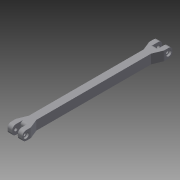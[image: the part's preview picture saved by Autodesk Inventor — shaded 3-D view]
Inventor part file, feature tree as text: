
AUTODESK INVENTOR PART (.ipt)
format: ipt  version: 2015 (Build 190159000, 159)  size: 167,424 bytes
history: native  units: mm
features: sketch x4, fillet x4, extrude x2, plane x2, mirror x2, loft x1, hole x1, other x1
ambient origin geometry x8: Origin, YZ Plane, XZ Plane, XY Plane, X Axis, Y Axis, Z Axis, Center Point
bodies: Solid1 (feature_tree)
feature tree (17):
  extrude  "Extrusion1"  Depth=10.0mm
  sketch  "Sketch2"  dims[d2=144.0mm d3=0.0mm d4=5.0mm]
  sketch  "Sketch3"  dims[d5=5.0mm d6=3.05mm d7=3.05mm d8=10.0mm]
  extrude  "Extrusion3"  Depth=5.0mm
  loft  "Loft2"
  plane  "Work Plane2"
  fillet  "Fillet4"  Radius=3.05mm
  fillet  "Fillet5"  Radius=10.0mm
  hole  "Hole1"  [1 undecoded]
  mirror  "Mirror2"
  plane  "Work Plane3"
  mirror  "Mirror3"
  fillet  "Fillet6"  [1 undecoded]
  fillet  "Fillet7"  Radius=4.0mm
  sketch  "Sketch1"  dims[d0=8.0mm d1=10.0mm]
  other  "Edges1"
  sketch  "Sketch5"  dims[d18=9.0mm d19=0.0mm d20=0.0mm d21=90.0deg d22=0.0mm d23=90.0deg d24=4.0mm d25=4.0mm d26=3.3mm d27=6.0mm d28=6.0mm d29=2.0mm d30=90.0deg d31=8.0mm d32=20.594885mm d42=3.0mm d43=3.0mm]
note: 2 required parameter values undecoded (feature->parameter linkage not recoverable at this tier; creation-order binding heuristic only, values carry confidence <= 0.55)
